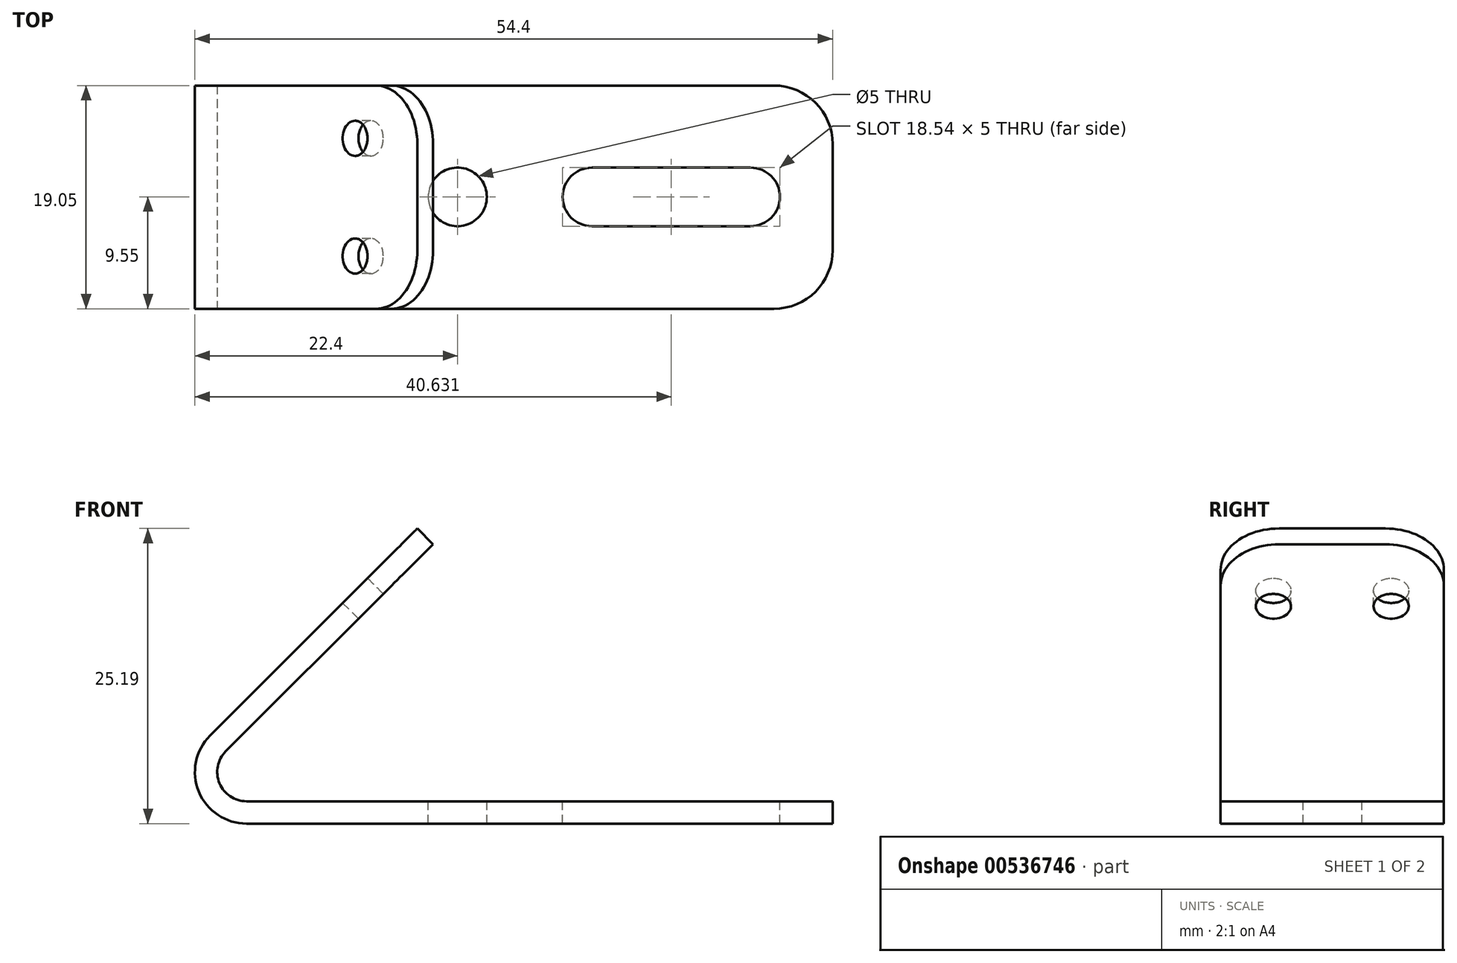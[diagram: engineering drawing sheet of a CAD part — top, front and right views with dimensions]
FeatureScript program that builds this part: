
annotation { "Feature Type Name" : "Feature", "Feature Type Description" : "" }
export const myFeature = defineFeature(function(context is Context, id is Id, definition is map)
    precondition{}
    {
        {
            var Q0;
            Q0=qCreatedBy(makeId("Front.planeOp"),FACE);
            var sketch = newSketch(context, id + "F0", { "sketchPlane" : qUnion([Q0])});
            skLineSegment(sketch, "E0", {"start": v(0, 0) * mm, "end": v(-50, 0) * mm});
            skArc(sketch, "E1", {"start": v(-53.11, 7.51) * mm, "mid": v(-54.07, 2.72) * mm, "end": v(-50, 0) * mm});
            skLineSegment(sketch, "E2", {"start": v(-53.11, 7.51) * mm, "end": v(-35.43, 25.19) * mm});
            skLineSegment(sketch, "E3", {"start": v(-35.43, 25.19) * mm, "end": v(-34.1, 23.85) * mm});
            skLineSegment(sketch, "E4", {"start": v(-34.1, 23.85) * mm, "end": v(-51.77, 6.17) * mm});
            skLineSegment(sketch, "E5", {"start": v(0, 0) * mm, "end": v(0, 1.9) * mm});
            skLineSegment(sketch, "E6", {"start": v(0, 1.9) * mm, "end": v(-50, 1.9) * mm});
            skArc(sketch, "E7", {"start": v(-51.77, 6.17) * mm, "mid": v(-52.3, 3.44) * mm, "end": v(-50, 1.9) * mm});
            skSolve(sketch);
        }
        {
            var Q0;
            Q0 = qSketchRegion(id + "F0", true);
            extrude(context, id + "F1", {"entities" : qUnion([Q0]), "oppositeDirection" : true, "depth" : 19.05 * mm, "offsetDistance" : 25.4 * mm});
        }
        {
            var Q0;
            Q0=makeQuery(id+"F1.opExtrude","SWEPT_FACE",FACE,{"disambiguationData":[OSD([sQuery(id+"F0.wireOp",EDGE,"E2")])]});
            var sketch = newSketch(context, id + "F2", { "sketchPlane" : qUnion([Q0])});
            skCircle(sketch, "E8", {"center": v(-14.55, -14.74) * mm, "radius": 1.5 * mm});
            skCircle(sketch, "E9", {"center": v(-4.5, -14.74) * mm, "radius": 1.5 * mm});
            skSolve(sketch);
        }
        {
            var Q0;
            Q0 = qSketchRegion(id + "F2", true);
            var Q1;
            Q1=makeQuery(id+"F1.opExtrude","SWEPT_FACE",FACE,{"disambiguationData":[OSD([sQuery(id+"F0.wireOp",EDGE,"E4")])]});
            extrude(context, id + "F3", {"entities" : qUnion([Q0]), "operationType" : NewBodyOperationType.REMOVE, "endBound" : BoundingType.UP_TO_SURFACE, "oppositeDirection" : true, "depth" : 2 * mm, "endBoundEntityFace" : qUnion([Q1]), "offsetDistance" : 25 * mm});
        }
        {
            var Q0;
            Q0=makeQuery(id+"F1.opExtrude","SWEPT_FACE",FACE,{"disambiguationData":[OSD([sQuery(id+"F0.wireOp",EDGE,"E6")])]});
            var sketch = newSketch(context, id + "F4", { "sketchPlane" : qUnion([Q0])});
            skArc(sketch, "E10", {"start": v(-20.54, 12.05) * mm, "mid": v(-23.04, 9.55) * mm, "end": v(-20.54, 7.05) * mm});
            skArc(sketch, "E11", {"start": v(-7, 7.05) * mm, "mid": v(-4.5, 9.55) * mm, "end": v(-7, 12.05) * mm});
            skLineSegment(sketch, "E12", {"start": v(-20.54, 12.05) * mm, "end": v(-7, 12.05) * mm});
            skLineSegment(sketch, "E13", {"start": v(-20.54, 7.05) * mm, "end": v(-7, 7.05) * mm});
            skCircle(sketch, "E14", {"center": v(-32, 9.55) * mm, "radius": 2.5 * mm});
            skSolve(sketch);
        }
        {
            var Q0;
            Q0 = qSketchRegion(id + "F4", true);
            extrude(context, id + "F5", {"entities" : qUnion([Q0]), "operationType" : NewBodyOperationType.REMOVE, "oppositeDirection" : true, "depth" : 25 * mm, "offsetDistance" : 25 * mm});
        }
        {
            var Q0;
            Q0=makeQuery(id+"F1.opExtrude","CAP_EDGE",EDGE,{"disambiguationData":[OSD([sQuery(id+"F0.wireOp",EDGE,"E3")])],"isStart":true});
            var Q1;
            Q1=makeQuery(id+"F1.opExtrude","CAP_EDGE",EDGE,{"disambiguationData":[OSD([sQuery(id+"F0.wireOp",EDGE,"E5")])],"isStart":true});
            var Q2;
            Q2=makeQuery(id+"F1.opExtrude","CAP_EDGE",EDGE,{"disambiguationData":[OSD([sQuery(id+"F0.wireOp",EDGE,"E3")])],"isStart":false});
            var Q3;
            Q3=makeQuery(id+"F1.opExtrude","CAP_EDGE",EDGE,{"disambiguationData":[OSD([sQuery(id+"F0.wireOp",EDGE,"E5")])],"isStart":false});
            fillet(context, id + "F6", {"entities" : qUnion([Q0, Q1, Q2, Q3]), "radius" : 5 * mm, "tangentPropagation" : true, "allowEdgeOverflow" : false});
        }
    });
